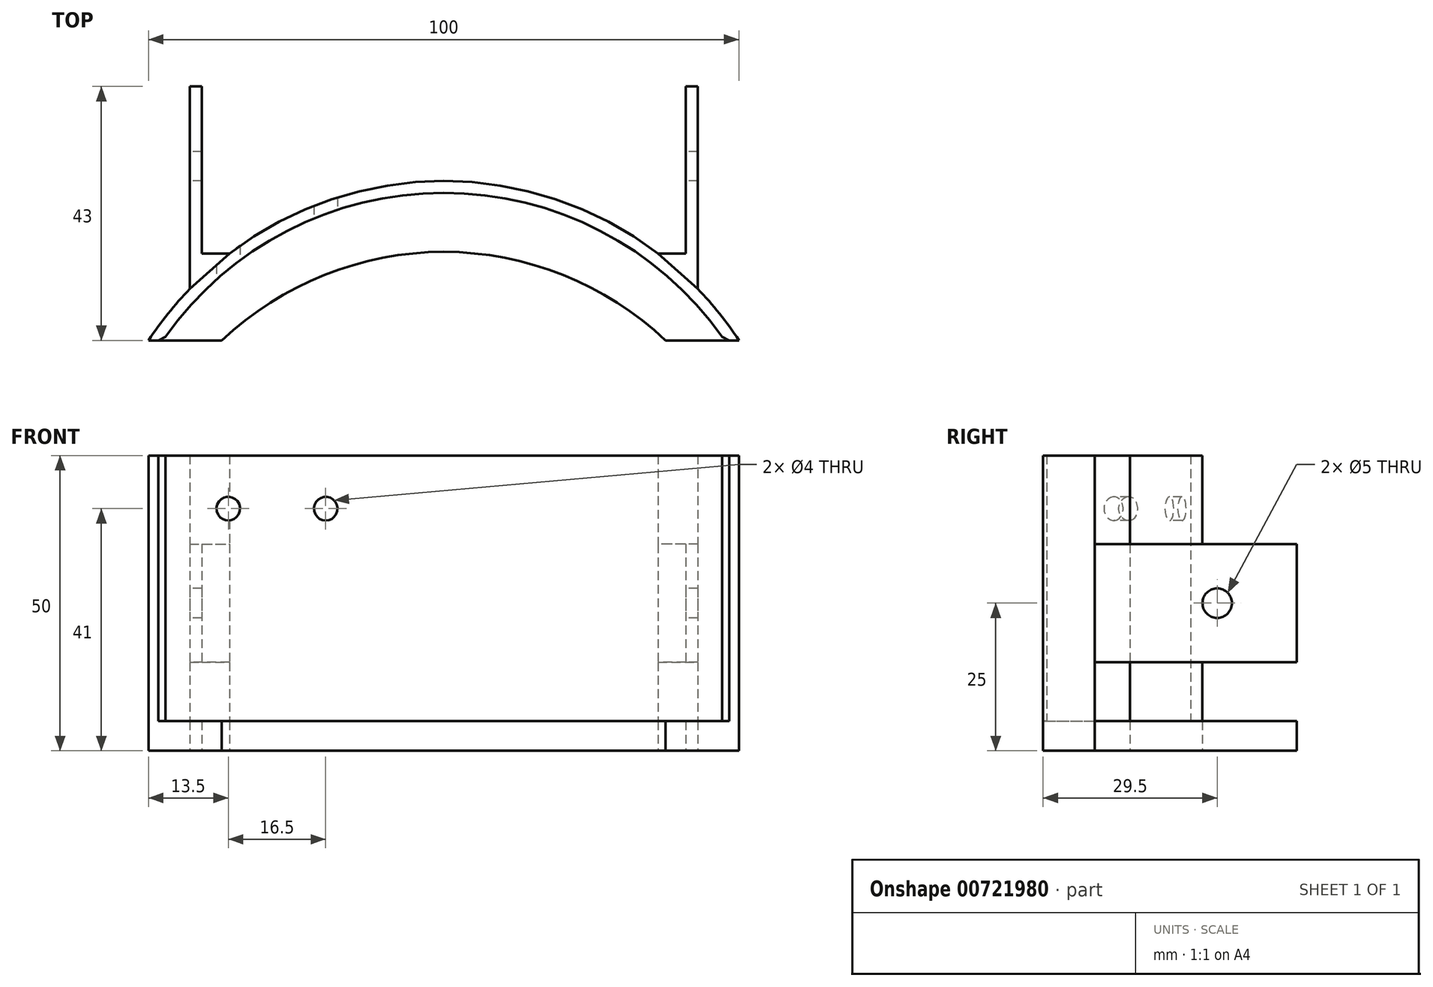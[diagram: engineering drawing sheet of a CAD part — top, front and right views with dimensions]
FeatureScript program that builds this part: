
annotation { "Feature Type Name" : "Feature", "Feature Type Description" : "" }
export const myFeature = defineFeature(function(context is Context, id is Id, definition is map)
    precondition{}
    {
        {
            var Q0;
            Q0=qCreatedBy(makeId("Top.planeOp"),FACE);
            var sketch = newSketch(context, id + "F0", { "sketchPlane" : qUnion([Q0])});
            skLineSegment(sketch, "E0", {"start": v(-50, 0) * mm, "end": v(-47.6, 0) * mm});
            skArc(sketch, "E1", {"start": v(50, 0) * mm, "mid": v(46.7, 4.54) * mm, "end": v(43, 8.76) * mm});
            skArc(sketch, "E2.0", {"start": v(47.6, 0) * mm, "mid": v(0, 25) * mm, "end": v(-47.6, 0) * mm});
            skLineSegment(sketch, "E3", {"start": v(50, 0) * mm, "end": v(47.6, 0) * mm});
            skLineSegment(sketch, "E4.trimOffspring", {"start": v(47.6, 0) * mm, "end": v(50, 0) * mm});
            skLineSegment(sketch, "E5.top", {"start": v(-43, 43) * mm, "end": v(-41, 43) * mm});
            skLineSegment(sketch, "E5.left", {"start": v(-43, 8.76) * mm, "end": v(-43, 43) * mm});
            skLineSegment(sketch, "E5.right", {"start": v(-41, 14.73) * mm, "end": v(-41, 43) * mm});
            skLineSegment(sketch, "E6", {"start": v(0, 49.02) * mm, "end": v(0, -14.9) * mm, "construction": true});
            skLineSegment(sketch, "E7.MirrorCS", {"start": v(43, 8.76) * mm, "end": v(43, 43) * mm});
            skLineSegment(sketch, "E8.MirrorCS", {"start": v(41, 14.73) * mm, "end": v(41, 43) * mm});
            skLineSegment(sketch, "E9.MirrorCS", {"start": v(43, 43) * mm, "end": v(41, 43) * mm});
            skPoint(sketch, "E10.orphan", {"position": v(-41, 8.76) * mm});
            skArc(sketch, "E11.trimOffspring", {"start": v(-43, 8.76) * mm, "mid": v(-46.7, 4.54) * mm, "end": v(-50, 0) * mm});
            skPoint(sketch, "E12.MirrorCS.end.orphan", {"position": v(41, 8.76) * mm});
            skPoint(sketch, "E12.MirrorCS.start.orphan", {"position": v(43, 8.76) * mm});
            skArc(sketch, "E13.trimOffspring", {"start": v(36.29, 14.73) * mm, "mid": v(0, 27) * mm, "end": v(-36.29, 14.73) * mm});
            skLineSegment(sketch, "E14", {"start": v(-41, 14.73) * mm, "end": v(-36.29, 14.73) * mm});
            skPoint(sketch, "E15.orphan", {"position": v(-41, 10.73) * mm});
            skLineSegment(sketch, "E16.MirrorCS", {"start": v(41, 14.73) * mm, "end": v(36.29, 14.73) * mm});
            skLineSegment(sketch, "E17", {"start": v(-47.6, 0) * mm, "end": v(-37.6, 0) * mm});
            skLineSegment(sketch, "E18", {"start": v(0, 25) * mm, "end": v(0, 15) * mm});
            skArc(sketch, "E19", {"start": v(0, 15) * mm, "mid": v(-20.22, 11.08) * mm, "end": v(-37.6, 0) * mm});
            skArc(sketch, "E20.MirrorCS", {"start": v(0, 15) * mm, "mid": v(20.22, 11.08) * mm, "end": v(37.6, 0) * mm});
            skLineSegment(sketch, "E21.MirrorCS", {"start": v(47.6, 0) * mm, "end": v(37.6, 0) * mm});
            skSolve(sketch);
        }
        {
            var Q0;
            Q0=makeQuery(id+"F0.imprint","IMPRINT",FACE,{"disambiguationData":[TD([[makeQuery(id+"F0.imprint","IMPRINT",EDGE,{"derivedFrom":sQuery(id+"F0.wireOp",EDGE,"E1")}),1.0]])]});
            extrude(context, id + "F1", {"entities" : qUnion([Q0]), "depth" : 50 * mm, "offsetDistance" : 25 * mm});
        }
        {
            var Q0;
            Q0=makeQuery(id+"F1.opExtrude","CAP_FACE",FACE,{"disambiguationData":[OSD([sQuery(id+"F0.wireOp",EDGE,"E1"),sQuery(id+"F0.wireOp",EDGE,"E2.0"),sQuery(id+"F0.wireOp",EDGE,"E0"),sQuery(id+"F0.wireOp",EDGE,"E4.trimOffspring"),sQuery(id+"F0.wireOp",EDGE,"E5.top"),sQuery(id+"F0.wireOp",EDGE,"E5.left"),sQuery(id+"F0.wireOp",EDGE,"E5.right"),sQuery(id+"F0.wireOp",EDGE,"E7.MirrorCS"),sQuery(id+"F0.wireOp",EDGE,"E8.MirrorCS"),sQuery(id+"F0.wireOp",EDGE,"E9.MirrorCS"),sQuery(id+"F0.wireOp",EDGE,"E11.trimOffspring"),sQuery(id+"F0.wireOp",EDGE,"E13.trimOffspring"),sQuery(id+"F0.wireOp",EDGE,"E14"),sQuery(id+"F0.wireOp",EDGE,"E16.MirrorCS")])],"isStart":false});
            var sketch = newSketch(context, id + "F2", { "sketchPlane" : qUnion([Q0])});
            skLineSegment(sketch, "E22", {"start": v(-36.29, 14.73) * mm, "end": v(-41, 14.73) * mm});
            skLineSegment(sketch, "E23", {"start": v(-41, 14.73) * mm, "end": v(-41, 43) * mm});
            skLineSegment(sketch, "E24", {"start": v(-41, 43) * mm, "end": v(-43, 43) * mm});
            skLineSegment(sketch, "E25", {"start": v(-43, 43) * mm, "end": v(-43, 8.76) * mm});
            skLineSegment(sketch, "E26", {"start": v(-43, 8.76) * mm, "end": v(-36.29, 14.73) * mm});
            skLineSegment(sketch, "E27", {"start": v(0, 52.59) * mm, "end": v(0, 4.53) * mm, "construction": true});
            skLineSegment(sketch, "E28.MirrorCS", {"start": v(41, 14.73) * mm, "end": v(41, 43) * mm});
            skLineSegment(sketch, "E29.MirrorCS", {"start": v(36.29, 14.73) * mm, "end": v(41, 14.73) * mm});
            skLineSegment(sketch, "E30.MirrorCS", {"start": v(43, 8.76) * mm, "end": v(36.29, 14.73) * mm});
            skLineSegment(sketch, "E31.MirrorCS", {"start": v(43, 43) * mm, "end": v(43, 8.76) * mm});
            skLineSegment(sketch, "E32.MirrorCS", {"start": v(41, 43) * mm, "end": v(43, 43) * mm});
            skSolve(sketch);
        }
        {
            var Q0;
            Q0 = qSketchRegion(id + "F2", true);
            extrude(context, id + "F3", {"entities" : qUnion([Q0]), "operationType" : NewBodyOperationType.REMOVE, "oppositeDirection" : true, "depth" : 15 * mm, "offsetDistance" : 25 * mm});
        }
        {
            var Q0;
            Q0=makeQuery(id+"F1.opExtrude","CAP_FACE",FACE,{"disambiguationData":[OSD([sQuery(id+"F0.wireOp",EDGE,"E1"),sQuery(id+"F0.wireOp",EDGE,"E2.0"),sQuery(id+"F0.wireOp",EDGE,"E0"),sQuery(id+"F0.wireOp",EDGE,"E4.trimOffspring"),sQuery(id+"F0.wireOp",EDGE,"E5.top"),sQuery(id+"F0.wireOp",EDGE,"E5.left"),sQuery(id+"F0.wireOp",EDGE,"E5.right"),sQuery(id+"F0.wireOp",EDGE,"E7.MirrorCS"),sQuery(id+"F0.wireOp",EDGE,"E8.MirrorCS"),sQuery(id+"F0.wireOp",EDGE,"E9.MirrorCS"),sQuery(id+"F0.wireOp",EDGE,"E11.trimOffspring"),sQuery(id+"F0.wireOp",EDGE,"E13.trimOffspring"),sQuery(id+"F0.wireOp",EDGE,"E14"),sQuery(id+"F0.wireOp",EDGE,"E16.MirrorCS")])],"isStart":true});
            var sketch = newSketch(context, id + "F4", { "sketchPlane" : qUnion([Q0])});
            skLineSegment(sketch, "E33", {"start": v(-43, -8.76) * mm, "end": v(-43, -43) * mm});
            skLineSegment(sketch, "E34", {"start": v(-43, -43) * mm, "end": v(-41, -43) * mm});
            skLineSegment(sketch, "E35", {"start": v(-41, -43) * mm, "end": v(-41, -14.73) * mm});
            skLineSegment(sketch, "E36", {"start": v(-41, -14.73) * mm, "end": v(-36.29, -14.73) * mm});
            skLineSegment(sketch, "E37", {"start": v(-36.29, -14.73) * mm, "end": v(-43, -8.76) * mm});
            skLineSegment(sketch, "E38", {"start": v(0, -2.79) * mm, "end": v(0, -51.5) * mm, "construction": true});
            skLineSegment(sketch, "E39.MirrorCS", {"start": v(36.29, -14.73) * mm, "end": v(43, -8.76) * mm});
            skLineSegment(sketch, "E40.MirrorCS", {"start": v(43, -8.76) * mm, "end": v(43, -43) * mm});
            skLineSegment(sketch, "E41.MirrorCS", {"start": v(41, -14.73) * mm, "end": v(36.29, -14.73) * mm});
            skLineSegment(sketch, "E42.MirrorCS", {"start": v(41, -43) * mm, "end": v(41, -14.73) * mm});
            skLineSegment(sketch, "E43.MirrorCS", {"start": v(43, -43) * mm, "end": v(41, -43) * mm});
            skSolve(sketch);
        }
        {
            var Q0;
            Q0 = qSketchRegion(id + "F4", true);
            extrude(context, id + "F5", {"entities" : qUnion([Q0]), "operationType" : NewBodyOperationType.REMOVE, "oppositeDirection" : true, "depth" : 15 * mm, "offsetDistance" : 25 * mm});
        }
        {
            var Q0;
            Q0=makeQuery(id+"F1.opExtrude","SWEPT_FACE",FACE,{"disambiguationData":[OSD([sQuery(id+"F0.wireOp",EDGE,"E5.left")])]});
            var sketch = newSketch(context, id + "F6", { "sketchPlane" : qUnion([Q0])});
            skCircle(sketch, "E44", {"center": v(-29.5, 25) * mm, "radius": 2.5 * mm});
            skSolve(sketch);
        }
        {
            var Q0;
            Q0=makeQuery(id+"F6.imprint","IMPRINT",FACE,{"disambiguationData":[TD([[makeQuery(id+"F6.imprint","IMPRINT",EDGE,{"derivedFrom":sQuery(id+"F6.wireOp",EDGE,"E44")}),1.0]])]});
            extrude(context, id + "F7", {"entities" : qUnion([Q0]), "operationType" : NewBodyOperationType.REMOVE, "endBound" : BoundingType.THROUGH_ALL, "oppositeDirection" : true, "depth" : 25 * mm, "offsetDistance" : 25 * mm});
        }
        {
            var Q0;
            Q0=makeQuery(id+"F1.opExtrude","SWEPT_EDGE",EDGE,{"disambiguationData":[OSD([sQuery(id+"F0.wireOp",EDGE,"E2.0"),sQuery(id+"F0.wireOp",EDGE,"E0")])]});
            var Q1;
            Q1=makeQuery(id+"F1.opExtrude","SWEPT_EDGE",EDGE,{"disambiguationData":[OSD([sQuery(id+"F0.wireOp",EDGE,"E2.0"),sQuery(id+"F0.wireOp",EDGE,"E4.trimOffspring")])]});
            chamfer(context, id + "F8", {"entities" : qUnion([Q0, Q1]), "width" : 1.5 * mm, "tangentPropagation" : true});
        }
        {
            var Q0;
            Q0 = qSketchRegion(id + "F0", true);
            extrude(context, id + "F9", {"entities" : qUnion([Q0]), "operationType" : NewBodyOperationType.ADD, "depth" : 5 * mm, "offsetDistance" : 25 * mm});
        }
        {
            var Q0;
            Q0=qCreatedBy(makeId("Front.planeOp"),FACE);
            var sketch = newSketch(context, id + "F10", { "sketchPlane" : qUnion([Q0])});
            skLineSegment(sketch, "E45", {"start": v(-103.86, 41) * mm, "end": v(99.12, 41) * mm, "construction": true});
            skLineSegment(sketch, "E46", {"start": v(0, 54.34) * mm, "end": v(0, -5.32) * mm, "construction": true});
            skPoint(sketch, "E47", {"position": v(-20, 41) * mm});
            skPoint(sketch, "E48", {"position": v(-36.5, 41) * mm});
            skCircle(sketch, "E49", {"center": v(-20, 41) * mm, "radius": 2 * mm});
            skCircle(sketch, "E50", {"center": v(-36.5, 41) * mm, "radius": 2 * mm});
            skLineSegment(sketch, "E51.MirrorCS", {"start": v(103.86, 41) * mm, "end": v(-99.12, 41) * mm, "construction": true});
            skCircle(sketch, "E52.MirrorC", {"center": v(36.5, 41) * mm, "radius": 2 * mm});
            skCircle(sketch, "E53.MirrorC", {"center": v(20, 41) * mm, "radius": 2 * mm});
            skSolve(sketch);
        }
        {
            var Q0;
            Q0=makeQuery(id+"F10.imprint","IMPRINT",FACE,{"disambiguationData":[TD([[makeQuery(id+"F10.imprint","IMPRINT",EDGE,{"derivedFrom":sQuery(id+"F10.wireOp",EDGE,"E50")}),1.0]])]});
            var Q1;
            Q1=makeQuery(id+"F10.imprint","IMPRINT",FACE,{"disambiguationData":[TD([[makeQuery(id+"F10.imprint","IMPRINT",EDGE,{"derivedFrom":sQuery(id+"F10.wireOp",EDGE,"E49")}),1.0]])]});
            var Q2;
            Q2=makeQuery(id+"F10.imprint","IMPRINT",FACE,{"disambiguationData":[TD([[makeQuery(id+"F10.imprint","IMPRINT",EDGE,{"derivedFrom":sQuery(id+"F10.wireOp",EDGE,"E53.MirrorC")}),-1.0]])]});
            var Q3;
            Q3=makeQuery(id+"F10.imprint","IMPRINT",FACE,{"disambiguationData":[TD([[makeQuery(id+"F10.imprint","IMPRINT",EDGE,{"derivedFrom":sQuery(id+"F10.wireOp",EDGE,"E52.MirrorC")}),-1.0]])]});
            extrude(context, id + "F11", {"entities" : qUnion([Q0, Q1, Q2, Q3]), "operationType" : NewBodyOperationType.REMOVE, "oppositeDirection" : true, "depth" : 33 * mm, "offsetDistance" : 25 * mm});
        }
    });
